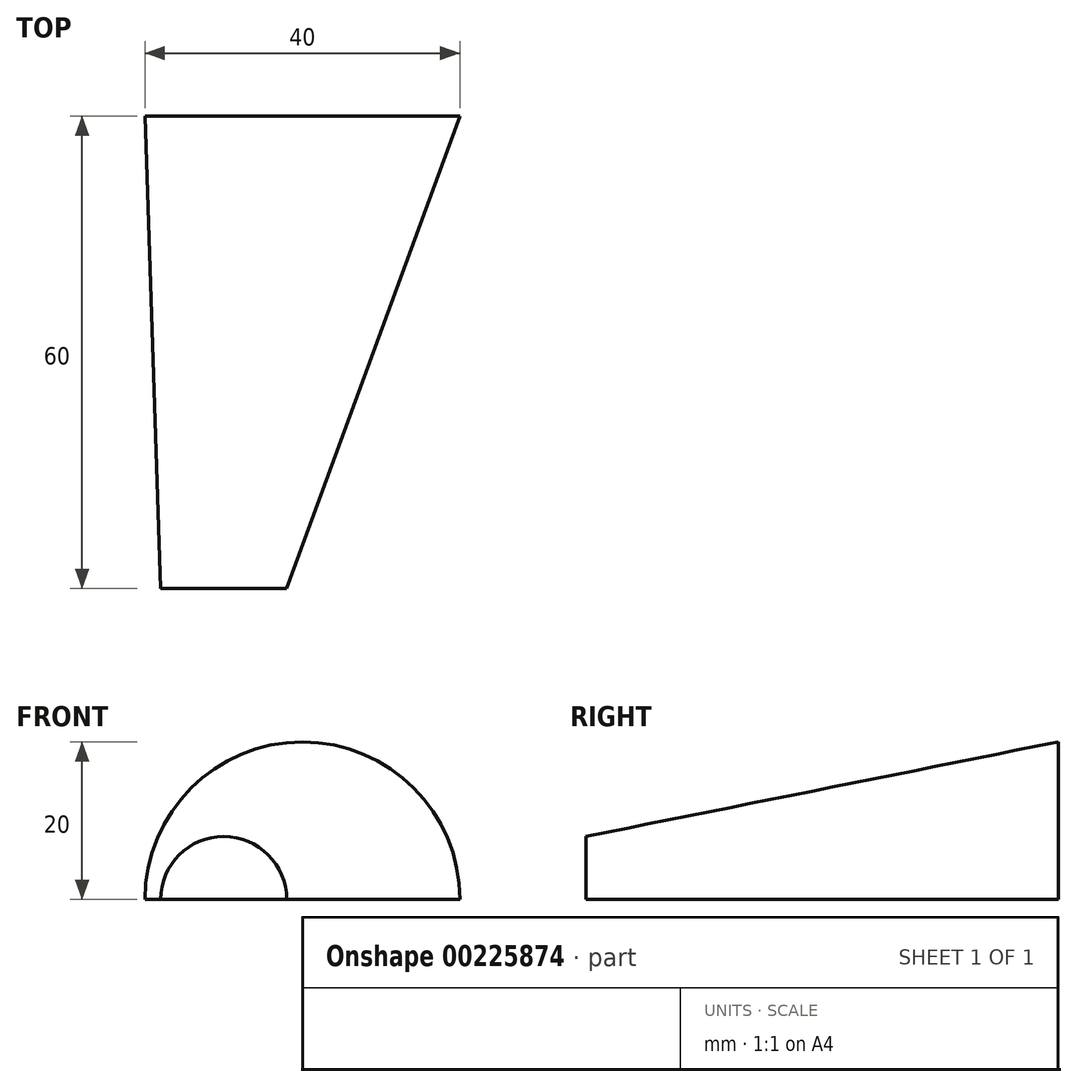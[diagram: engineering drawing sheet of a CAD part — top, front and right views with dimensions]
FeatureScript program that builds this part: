
annotation { "Feature Type Name" : "Feature", "Feature Type Description" : "" }
export const myFeature = defineFeature(function(context is Context, id is Id, definition is map)
    precondition{}
    {
        {
            var Q0;
            Q0=qCreatedBy(makeId("Front.planeOp"),FACE);
            var sketch = newSketch(context, id + "F0", { "sketchPlane" : qUnion([Q0])});
            skLineSegment(sketch, "E0", {"start": v(-10, 15.94) * mm, "end": v(-10, -13.92) * mm, "construction": true});
            skArc(sketch, "E1", {"start": v(-2, 0) * mm, "mid": v(-10, 8) * mm, "end": v(-18, 0) * mm});
            skPoint(sketch, "E1.centerSnap0", {"position": v(-10, 1) * mm});
            skPoint(sketch, "E2.orphan", {"position": v(-10, -13.92) * mm});
            skPoint(sketch, "E3", {"position": v(-18, 0) * mm});
            skPoint(sketch, "E4", {"position": v(-2, 0) * mm});
            skLineSegment(sketch, "E5", {"start": v(-18, 0) * mm, "end": v(-2, 0) * mm});
            skSolve(sketch);
        }
        {
            var Q0;
            Q0=qCreatedBy(makeId("Front.planeOp"),FACE);
            cPlane(context, id + "F1", {"entities" : qUnion([Q0]), "cplaneType" : CPlaneType.OFFSET, "offset" : 60 * mm, "oppositeDirection" : true, "width" : 150 * mm, "height" : 150 * mm});
        }
        {
            var Q0;
            Q0=qCreatedBy(id+"F1.planeOp",FACE);
            var sketch = newSketch(context, id + "F2", { "sketchPlane" : qUnion([Q0])});
            skArc(sketch, "E6", {"start": v(20, 0) * mm, "mid": v(0, 20) * mm, "end": v(-20, 0) * mm});
            skLineSegment(sketch, "E7", {"start": v(-20, 0) * mm, "end": v(20, 0) * mm});
            skSolve(sketch);
        }
        {
            var Q0;
            Q0 = qSketchRegion(id + "F0", true);
            var Q1;
            Q1 = qSketchRegion(id + "F2", true);
            loft(context, id + "F3", {"sheetProfilesArray" : [{ "sheetProfileEntities" : qUnion([Q0]) }, { "sheetProfileEntities" : qUnion([Q1]) }]});
        }
    });
